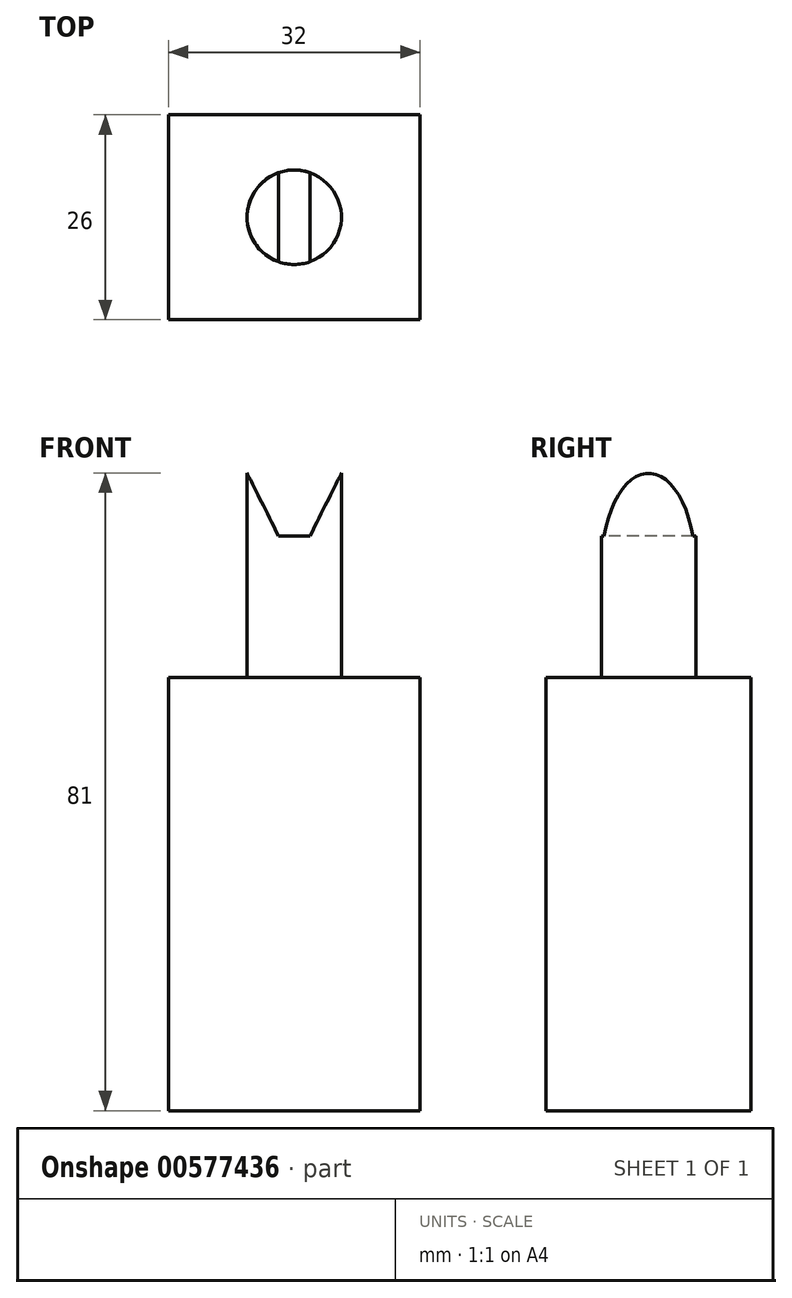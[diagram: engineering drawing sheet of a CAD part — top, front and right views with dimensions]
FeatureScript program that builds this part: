
annotation { "Feature Type Name" : "Feature", "Feature Type Description" : "" }
export const myFeature = defineFeature(function(context is Context, id is Id, definition is map)
    precondition{}
    {
        {
            var Q0;
            Q0=qCreatedBy(makeId("Top.planeOp"),FACE);
            var sketch = newSketch(context, id + "F0", { "sketchPlane" : qUnion([Q0])});
            skLineSegment(sketch, "E0.bottom", {"start": v(0, 0) * mm, "end": v(32, 0) * mm});
            skLineSegment(sketch, "E0.top", {"start": v(0, 26) * mm, "end": v(32, 26) * mm});
            skLineSegment(sketch, "E0.left", {"start": v(0, 0) * mm, "end": v(0, 26) * mm});
            skLineSegment(sketch, "E0.right", {"start": v(32, 0) * mm, "end": v(32, 26) * mm});
            skSolve(sketch);
        }
        {
            var Q0;
            Q0 = qSketchRegion(id + "F0", true);
            extrude(context, id + "F1", {"entities" : qUnion([Q0]), "depth" : 55 * mm, "offsetDistance" : 25 * mm});
        }
        {
            var Q0;
            Q0=makeQuery(id+"F1.opExtrude","CAP_FACE",FACE,{"disambiguationData":[OSD([sQuery(id+"F0.wireOp",EDGE,"E0.bottom"),sQuery(id+"F0.wireOp",EDGE,"E0.top"),sQuery(id+"F0.wireOp",EDGE,"E0.left"),sQuery(id+"F0.wireOp",EDGE,"E0.right")])],"isStart":false});
            var sketch = newSketch(context, id + "F2", { "sketchPlane" : qUnion([Q0])});
            skCircle(sketch, "E1", {"center": v(16, 13) * mm, "radius": 6 * mm});
            skSolve(sketch);
        }
        {
            var Q0;
            Q0 = qSketchRegion(id + "F2", true);
            extrude(context, id + "F3", {"entities" : qUnion([Q0]), "operationType" : NewBodyOperationType.ADD, "depth" : 26 * mm, "offsetDistance" : 25 * mm});
        }
        {
            var Q0;
            Q0=makeQuery(id+"F1.opExtrude","SWEPT_FACE",FACE,{"disambiguationData":[OSD([sQuery(id+"F0.wireOp",EDGE,"E0.bottom")])]});
            var sketch = newSketch(context, id + "F4", { "sketchPlane" : qUnion([Q0])});
            skLineSegment(sketch, "E2", {"start": v(10, 81) * mm, "end": v(14, 73) * mm});
            skLineSegment(sketch, "E3", {"start": v(14, 73) * mm, "end": v(18, 73) * mm});
            skLineSegment(sketch, "E4", {"start": v(18, 73) * mm, "end": v(22, 81) * mm});
            skLineSegment(sketch, "E5", {"start": v(10, 81) * mm, "end": v(22, 81) * mm});
            skSolve(sketch);
        }
        {
            var Q0;
            Q0=makeQuery(id+"F4.imprint","IMPRINT",FACE,{"disambiguationData":[TD([[makeQuery(id+"F4.imprint","IMPRINT",EDGE,{"derivedFrom":sQuery(id+"F4.wireOp",EDGE,"E2")}),1.0]])]});
            extrude(context, id + "F5", {"entities" : qUnion([Q0]), "operationType" : NewBodyOperationType.REMOVE, "oppositeDirection" : true, "depth" : 25 * mm, "offsetDistance" : 25 * mm});
        }
    });
